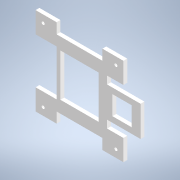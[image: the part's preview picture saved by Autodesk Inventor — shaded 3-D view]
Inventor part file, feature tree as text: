
AUTODESK INVENTOR PART (.ipt)
format: ipt  version: 2020 (Build 240168000, 168)  size: 177,152 bytes
history: native  units: in
note: dims shown in document units (in); Inventor stores cm internally (conversion verified against a paired STEP export)
features: reference x14, other x9, extrude x1, sketch x1
ambient origin geometry x8: Origin, YZ Plane, XZ Plane, XY Plane, X Axis, Y Axis, Z Axis, Center Point
bodies: Body1 (feature_tree)
feature tree (25):
  extrude  "Extrusion3"  Depth=0.5in
  sketch  "Sketch1"  dims[d1=0.5in d2=0.5in d4=0.55in d5=0.55in d6=0.55in d7=0.55in d8=0.55in d9=0.55in d10=0.55in d11=0.55in d20=0.5in d21=0.5in d22=0.1in d23=0.0in d26=0.15in]
  reference  "Reference1"
  reference  "Reference2"
  reference  "Reference3"
  reference  "Reference4"
  reference  "Reference5"
  reference  "Reference6"
  reference  "Reference7"
  reference  "Reference8"
  reference  "Reference9"
  reference  "Reference10"
  reference  "Reference11"
  reference  "Reference12"
  reference  "Reference13"
  reference  "Reference14"
  other  "<userpath>\Documents\Inventor\Drone\Assembly.iam"
  other  "Assembly.iam"
  other  "Frame:1"
  other  "F330 Top plate2 v1:1"
  other  "Part5:1"
  other  "VibrationDampener:2"
  other  "VibrationDampener:1"
  other  "DJI F330 qoadrotor arm:3"
  other  "DJI F330 qoadrotor arm v2"
